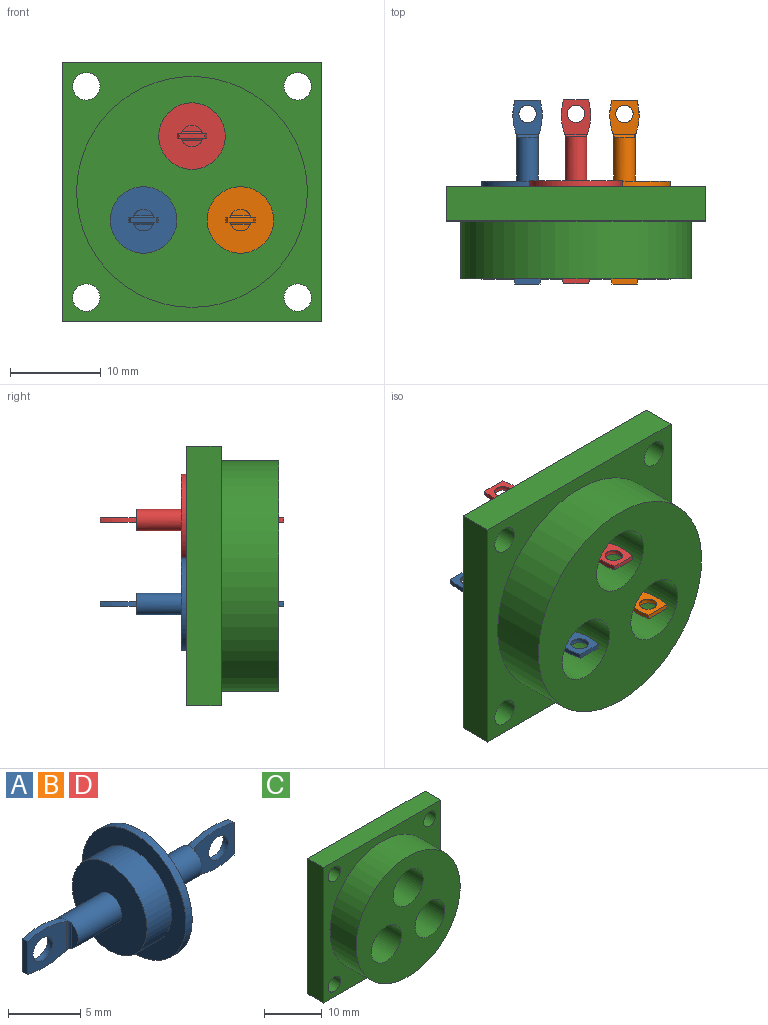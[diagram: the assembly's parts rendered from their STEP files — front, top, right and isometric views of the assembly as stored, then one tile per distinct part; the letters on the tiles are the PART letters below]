
ASSEMBLY  parts=4 mates=3
PART A: 27 faces, bbox 20.3x10.2x10.2 mm
  f0: revolved ~3.97x0.86mm, area 2.1mm2, adj f10,f12,f18,f21,f25,f26
  f1: plane 2.79x0.51mm, normal (1,0,0), area 1.4mm2, adj f2,f3,f13,f16
  f2: revolved ~3.97x0.86mm, area 2.1mm2, adj f1,f4,f13,f16,f23,f24
  f3: revolved ~3.97x0.86mm, area 2.1mm2, adj f1,f4,f13,f16,f23,f24
  f4: cylinder r=1.18mm len=4.95mm, axis (-1,0,0), area 36.2mm2, adj f2,f3,f5,f14,f15,f23,f24
  f5: plane 10.16x10.16mm, normal (1,0,0), area 76.7mm2, adj f4,f6
  f6: cylinder r=5.08mm len=10.16mm, axis (-1,0,0), area 19.5mm2, adj f5,f7
  f7: plane 10.16x10.16mm, normal (-1,0,0), area 39mm2, adj f6,f8
  f8: cylinder r=3.66mm len=7.32mm, axis (-1,0,0), area 54.9mm2, adj f7,f9
  f9: plane 7.32x7.32mm, normal (-1,0,0), area 37.6mm2, adj f8,f10
  f10: cylinder r=1.18mm len=4.36mm, axis (-1,0,0), area 31.8mm2, adj f0,f9,f11,f19,f20,f25,f26
  f11: revolved ~3.97x0.86mm, area 2.1mm2, adj f10,f12,f18,f21,f25,f26
  f12: plane 2.79x0.51mm, normal (-1,0,0), area 1.4mm2, adj f0,f11,f18,f21
  f13: plane 3.82x3.23mm, normal (0,1,0), area 8.6mm2, adj f1,f2,f3,f17,f23
  f14: plane 2.13x0.67mm, normal (1,0,0), area 1mm2, adj f4,f23
  f15: plane 2.13x0.67mm, normal (1,0,0), area 1mm2, adj f4,f24
  f16: plane 3.82x3.23mm, normal (0,-1,0), area 8.6mm2, adj f1,f2,f3,f17,f24
  f17: sphere r=0.99mm, area 3.2mm2, adj f13,f16
  f18: plane 3.82x3.23mm, normal (0,1,0), area 8.6mm2, adj f0,f11,f12,f22,f26
  f19: plane 2.13x0.67mm, normal (-1,0,0), area 1mm2, adj f10,f26
  f20: plane 2.13x0.67mm, normal (-1,0,0), area 1mm2, adj f10,f25
  f21: plane 3.82x3.23mm, normal (0,-1,0), area 8.6mm2, adj f0,f11,f12,f22,f25
  f22: sphere r=0.99mm, area 3.2mm2, adj f18,f21
  f23: cylinder r=0.25mm len=2.43mm, axis (0,0,-1), area 0.9mm2, adj f2,f3,f4,f13,f14
  f24: cylinder r=0.25mm len=2.43mm, axis (0,0,1), area 0.9mm2, adj f2,f3,f4,f15,f16
  f25: cylinder r=0.25mm len=2.43mm, axis (0,0,-1), area 0.9mm2, adj f0,f10,f11,f20,f21
  f26: cylinder r=0.25mm len=2.43mm, axis (0,0,1), area 0.9mm2, adj f0,f10,f11,f18,f19
PART B: same geometry as A
PART C: 15 faces, bbox 28.6x10.2x28.6 mm
  f0: cylinder r=3.66mm len=10.16mm, axis (0,1,0), area 233.5mm2, adj f4,f13
  f1: cylinder r=3.66mm len=10.16mm, axis (0,1,0), area 233.5mm2, adj f4,f13
  f2: cylinder r=3.66mm len=10.16mm, axis (0,1,0), area 233.5mm2, adj f4,f13
  f3: cylinder r=12.7mm len=25.4mm, axis (0,1,0), area 506.7mm2, adj f4,f14
  f4: plane 25.4x25.4mm, normal (0,-1,0), area 380.6mm2, adj f0,f1,f2,f3
  f5: plane 28.58x3.81mm, normal (0,0,1), area 108.9mm2, adj f6,f12,f13,f14
  f6: plane 28.58x3.81mm, normal (-1,0,0), area 108.9mm2, adj f5,f7,f13,f14
  f7: plane 28.58x3.81mm, normal (0,0,-1), area 108.9mm2, adj f6,f12,f13,f14
  f8: cylinder r=1.51mm len=3.81mm, axis (0,-1,0), area 36.2mm2, adj f13,f14
  f9: cylinder r=1.51mm len=3.81mm, axis (0,-1,0), area 36.2mm2, adj f13,f14
  f10: cylinder r=1.51mm len=3.81mm, axis (0,-1,0), area 36.2mm2, adj f13,f14
  f11: cylinder r=1.51mm len=3.81mm, axis (0,-1,0), area 36.2mm2, adj f13,f14
  f12: plane 28.58x3.81mm, normal (1,0,0), area 108.9mm2, adj f5,f7,f13,f14
  f13: plane 28.58x28.58mm, normal (0,1,0), area 661.7mm2, adj f0,f1,f2,f5,f6,f7,f8,f9
  f14: plane 28.58x28.58mm, normal (0,-1,0), area 281.1mm2, adj f3,f5,f6,f7,f8,f9,f10,f11
PART D: same geometry as A
PLACE A rot(axis=(0.58,0.58,0.58),120deg) t=(-5.33,3.21,-3.08)mm
PLACE B rot(axis=(0.58,0.58,0.58),120deg) t=(5.33,3.21,-3.08)mm
PLACE C at identity fixed
PLACE D rot(axis=(0.58,0.58,0.58),120deg) t=(0,3.21,6.16)mm
MATE fastened D.f4 <-> C.f2  axis (0,-1,0) through (0,3.81,6.16)mm
MATE fastened B.f4 <-> C.f0  axis (0,-1,0) through (5.33,3.81,-3.08)mm
MATE fastened A.f4 <-> C.f1  axis (0,-1,0) through (-5.33,3.81,-3.08)mm
